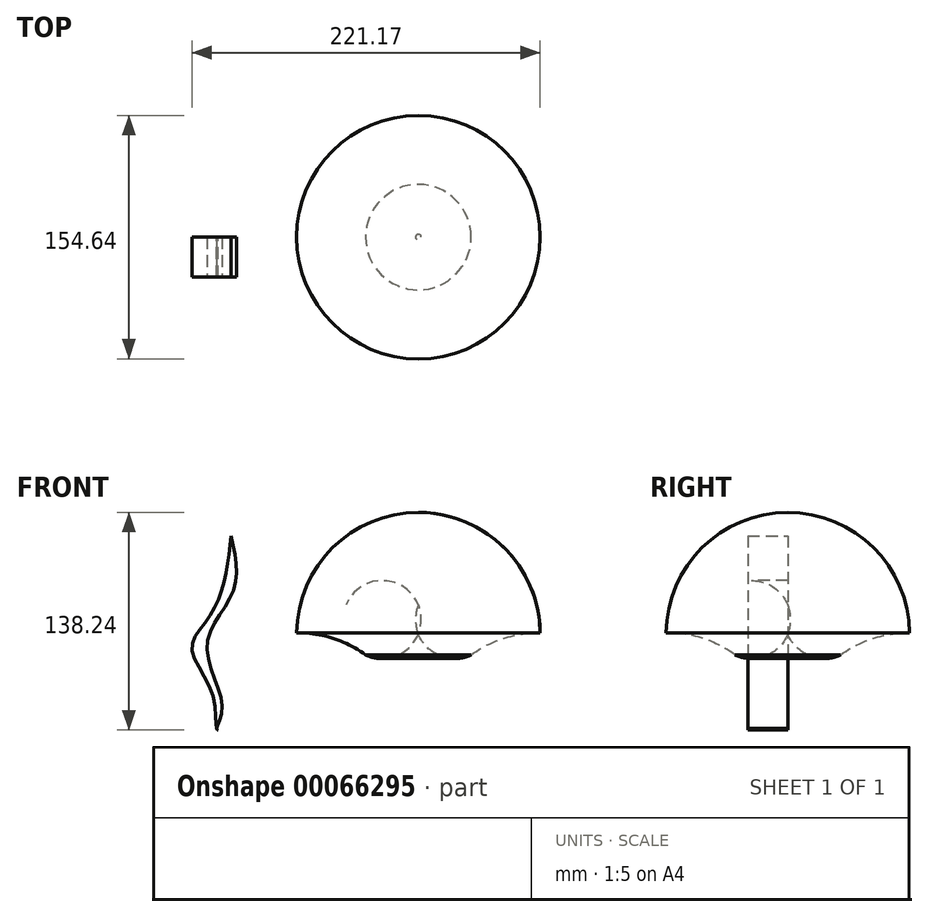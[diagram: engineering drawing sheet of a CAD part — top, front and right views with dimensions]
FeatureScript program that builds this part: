
annotation { "Feature Type Name" : "Feature", "Feature Type Description" : "" }
export const myFeature = defineFeature(function(context is Context, id is Id, definition is map)
    precondition{}
    {
        {
            var Q0;
            Q0=qCreatedBy(makeId("Front.planeOp"),FACE);
            var sketch = newSketch(context, id + "F0", { "sketchPlane" : qUnion([Q0])});
            skArc(sketch, "E0", {"start": v(153.52, 13.99) * mm, "mid": v(69.18, 90.16) * mm, "end": v(0, 0) * mm});
            skArc(sketch, "E1", {"start": v(76.2, 13.16) * mm, "mid": v(90.12, -0.63) * mm, "end": v(109.7, 0) * mm});
            skArc(sketch, "E2", {"start": v(153.52, 13.99) * mm, "mid": v(130.48, 10.52) * mm, "end": v(109.7, 0) * mm});
            skLineSegment(sketch, "E3", {"start": v(76.2, 13.16) * mm, "end": v(76.2, 90.48) * mm});
            skSolve(sketch);
        }
        {
            var Q0;
            Q0=makeQuery(id+"F0.imprint","IMPRINT",FACE,{"disambiguationData":[TD([[makeQuery(id+"F0.imprint","IMPRINT",EDGE,{"derivedFrom":sQuery(id+"F0.wireOp",EDGE,"E1")}),1.0]])]});
            var Q1;
            Q1=sQuery(id+"F0.wireOp",EDGE,"E3");
            revolve(context, id + "F1", {"entities" : qUnion([Q0]), "axis" : qUnion([Q1]), "revolveType" : RevolveType.FULL});
        }
        {
            var Q0;
            Q0=qCreatedBy(makeId("Front.planeOp"),FACE);
            var sketch = newSketch(context, id + "F2", { "sketchPlane" : qUnion([Q0])});
            skFitSpline(sketch, "E4", {"points": [v(-42.7, 75.57) * mm, v(-41.55, 40.21) * mm, v(-58.06, 6.28) * mm, v(-48.46, -33.17) * mm, v(-51.91, -46.83) * mm, v(-51.15, -47.76) * mm], "startDerivative": vector(30.88, -143.12) * mm, "endDerivative": vector(23.12, -13.35) * mm});
            skFitSpline(sketch, "E5", {"points": [v(-42.7, 75.57) * mm, v(-46.93, 47.49) * mm, v(-57.67, 22.5) * mm, v(-67.65, 4.28) * mm, v(-54.99, -23.92) * mm, v(-51.91, -46.83) * mm, v(-51.15, -47.76) * mm], "startDerivative": vector(-14.63, -141.51) * mm, "endDerivative": vector(20.76, -12.18) * mm});
            skSolve(sketch);
        }
        {
            var Q0;
            Q0 = qSketchRegion(id + "F2", true);
            extrude(context, id + "F3", {"entities" : qUnion([Q0]), "depth" : 25.4 * mm});
        }
    });
